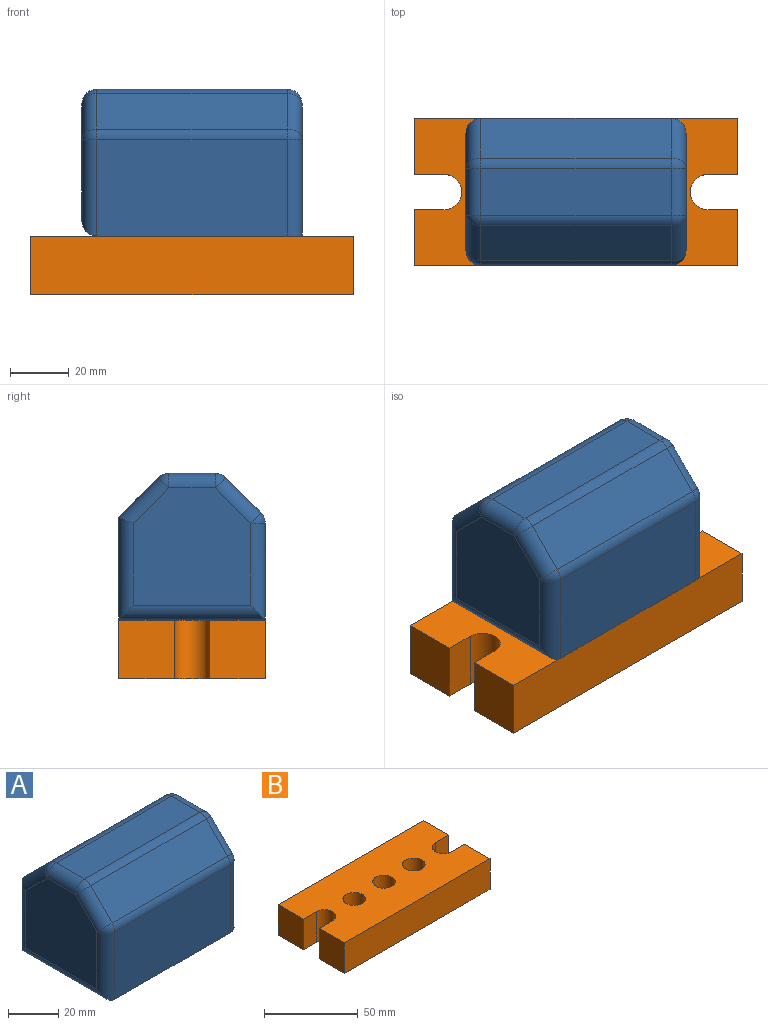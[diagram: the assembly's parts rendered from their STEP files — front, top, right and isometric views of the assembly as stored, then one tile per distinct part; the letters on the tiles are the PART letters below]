
ASSEMBLY  parts=2 mates=1
PART A: 34 faces, bbox 75x50x50 mm
  f0: plane 65x32.93mm, normal (0,-1,0), area 2140.4mm2, adj f5,f28,f29,f33
  f1: plane 45x40mm, normal (1,0,0), area 1654.3mm2, adj f5,f14,f15,f20,f27,f28
  f2: plane 65x35mm, normal (0,1,0), area 2275mm2, adj f5,f12,f14,f21
  f3: plane 40x40mm, normal (-1,0,0), area 1454.3mm2, adj f18,f21,f22,f25,f29,f30
  f4: plane 65x15.86mm, normal (0,0,1), area 1030.8mm2, adj f16,f20,f22,f23
  f5: plane 70x50mm, normal (0,0,-1), area 3253.7mm2, adj f0,f1,f2,f6,f8,f10,f14,f25
  f6: cylinder r=5mm len=25mm, axis (0,0,-1), area 785.4mm2, adj f5,f7
  f7: plane 10x10mm, normal (0,0,-1), area 78.5mm2, adj f6
  f8: cylinder r=5mm len=25mm, axis (0,0,-1), area 785.4mm2, adj f5,f9
  f9: plane 10x10mm, normal (0,0,-1), area 78.5mm2, adj f8
  f10: cylinder r=5mm len=25mm, axis (0,0,-1), area 785.4mm2, adj f5,f11
  f11: plane 10x10mm, normal (0,0,-1), area 78.5mm2, adj f10
  f12: plane 65x13.54mm, normal (0,0.71,0.71), area 1244.2mm2, adj f2,f15,f16,f18
  f13: plane 65x12.07mm, normal (0,-0.71,0.71), area 1109.6mm2, adj f23,f27,f30,f33
  f14: cylinder r=5mm len=35mm, axis (0,0,-1), area 269mm2, adj f1,f2,f5,f15
  f15: cylinder r=5mm len=17.07mm, axis (0,0.71,-0.71), area 144.4mm2, adj f1,f12,f14,f17
  f16: cylinder r=5mm len=65mm, axis (-1,0,0), area 255.3mm2, adj f4,f12,f17,f19
  f17: sphere r=5mm, area 19.6mm2, adj f15,f16,f20
  f18: cylinder r=5mm len=17.07mm, axis (0,0.71,-0.71), area 144.4mm2, adj f3,f12,f19,f21
  f19: sphere r=5mm, area 19.6mm2, adj f16,f18,f22
  f20: cylinder r=5mm len=15.86mm, axis (0,-1,0), area 124.5mm2, adj f1,f4,f17,f24
  f21: cylinder r=5mm len=35mm, axis (0,0,1), area 254.7mm2, adj f2,f3,f18,f25
  f22: cylinder r=5mm len=15.86mm, axis (0,1,0), area 124.5mm2, adj f3,f4,f19,f26
  f23: cylinder r=5mm len=65mm, axis (-1,0,0), area 255.3mm2, adj f4,f13,f24,f26
  f24: sphere r=5mm, area 19.6mm2, adj f20,f23,f27
  f25: cylinder r=5mm len=50mm, axis (0,-1,0), area 364.2mm2, adj f3,f5,f21,f29
  f26: sphere r=5mm, area 19.6mm2, adj f22,f23,f30
  f27: cylinder r=5mm len=15.61mm, axis (0,-0.71,-0.71), area 134.1mm2, adj f1,f13,f24,f31
  f28: cylinder r=5mm len=32.93mm, axis (0,0,1), area 258.6mm2, adj f0,f1,f5,f31
  f29: cylinder r=5mm len=32.93mm, axis (0,0,-1), area 244.4mm2, adj f0,f3,f25,f32
  f30: cylinder r=5mm len=15.61mm, axis (0,-0.71,-0.71), area 134.1mm2, adj f3,f13,f26,f32
  f31: sphere r=5mm, area 19.6mm2, adj f27,f28,f33
  f32: sphere r=5mm, area 19.6mm2, adj f29,f30,f33
  f33: cylinder r=5mm len=65mm, axis (1,0,0), area 255.3mm2, adj f0,f13,f31,f32
PART B: 23 faces, bbox 110x50x20 mm
  f0: plane 20x10mm, normal (0,1,0), area 200mm2, adj f1,f11,f12,f13
  f1: plane 20x19mm, normal (-1,0,0), area 380mm2, adj f0,f2,f12,f13
  f2: plane 110x20mm, normal (0,-1,0), area 2200mm2, adj f1,f3,f12,f13
  f3: plane 20x19mm, normal (1,0,0), area 380mm2, adj f2,f4,f12,f13
  f4: plane 20x10mm, normal (0,1,0), area 200mm2, adj f3,f5,f12,f13
  f5: cylinder r=6mm len=20mm, axis (0,0,1), area 377mm2, adj f4,f6,f12,f13
  f6: plane 20x10mm, normal (0,-1,0), area 200mm2, adj f5,f7,f12,f13
  f7: plane 20x19mm, normal (1,0,0), area 380mm2, adj f6,f8,f12,f13
  f8: plane 110x20mm, normal (0,1,0), area 2200mm2, adj f7,f9,f12,f13
  f9: plane 20x19mm, normal (-1,0,0), area 380mm2, adj f8,f10,f12,f13
  f10: plane 20x10mm, normal (0,-1,0), area 200mm2, adj f9,f11,f12,f13
  f11: cylinder r=6mm len=20mm, axis (0,0,1), area 377mm2, adj f0,f10,f12,f13
  f12: plane 110x50mm, normal (0,0,-1), area 4911.3mm2, adj f0,f1,f2,f3,f4,f5,f6,f7
  f13: plane 110x50mm, normal (0,0,1), area 4807.6mm2, adj f0,f1,f2,f3,f4,f5,f6,f7
  f14: cylinder r=6mm len=15mm, axis (0,0,1), area 565.5mm2, adj f13,f15
  f15: plane 12x12mm, normal (0,0,1), area 34.6mm2, adj f14,f22
  f16: cylinder r=6mm len=15mm, axis (0,0,1), area 565.5mm2, adj f13,f17
  f17: plane 12x12mm, normal (0,0,1), area 34.6mm2, adj f16,f21
  f18: cylinder r=6mm len=15mm, axis (0,0,1), area 565.5mm2, adj f13,f19
  f19: plane 12x12mm, normal (0,0,1), area 34.6mm2, adj f18,f20
  f20: cylinder r=5mm len=10mm, axis (0,0,1), area 157.1mm2, adj f12,f19
  f21: cylinder r=5mm len=10mm, axis (0,0,1), area 157.1mm2, adj f12,f17
  f22: cylinder r=5mm len=10mm, axis (0,0,1), area 157.1mm2, adj f12,f15
PLACE A at identity
PLACE B at identity
MATE fastened A.f8 <-> B.f16  axis (0,0,-1) through (0,0,0)mm
